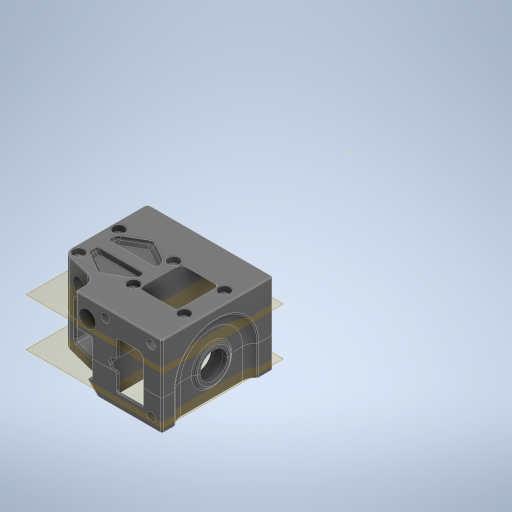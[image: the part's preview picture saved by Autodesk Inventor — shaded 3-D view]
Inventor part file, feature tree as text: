
AUTODESK INVENTOR PART (.ipt)
format: ipt  version: 2023 (Build 270158000, 158)  size: 2,304,000 bytes
history: native  units: mm
features: sketch x6, other x5, plane x3, extrude x2, loft x2
ambient origin geometry x8: Origin, YZ Plane, XZ Plane, XY Plane, X Axis, Y Axis, Z Axis, Center Point
bodies: Solid1 (feature_tree), Solid2 (feature_tree)
feature tree (18):
  sketch  "Sketch1"  dims[d1=1.25mm d2=3.0mm]
  plane  "Work Plane1"
  extrude  "Frame Sensor hole Part 2"  Depth=3.0mm
  plane  "Work Plane2"
  extrude  "Frame Sensor hole Part 3"  [1 undecoded]
  plane  "Work Plane3"
  sketch  "Sketch5"  dims[d11=4.75mm d12=-7.25mm]
  sketch  "Sketch6"  dims[d13=2.4mm]
  sketch  "Sketch11"  dims[d14=3.0mm d15=64.0mm d16=0.0mm d21=2.4mm d22=-25.25mm d23=2.5mm d42=0.0mm d43=90.0deg d44=0.0mm d45=90.0deg d46=0.0mm d47=90.0deg d48=3.0mm d49=0.0mm d50=90.0deg d51=0.0mm d52=90.0deg d53=0.0mm d54=90.0deg d38=0.5mm d39=50.0mm d40=0.5mm d41=50.0mm]
  loft  "Frame Sensor second curve"
  loft  "Frame Sensor first curve"
  sketch  "Sketch2"  dims[d5=10.0mm d6=-12.5mm]
  sketch  "Sketch3"  dims[d8=3.0mm d9=25.25mm d10=0.0mm]
  other  "Edges4"
  other  "Edges5"
  other  "Edges6"
  other  "z_drive_main_a_x2"
  other  "z_drive_retainer_a_x2"
note: 1 required parameter value undecoded (feature->parameter linkage not recoverable at this tier; creation-order binding heuristic only, values carry confidence <= 0.55)
